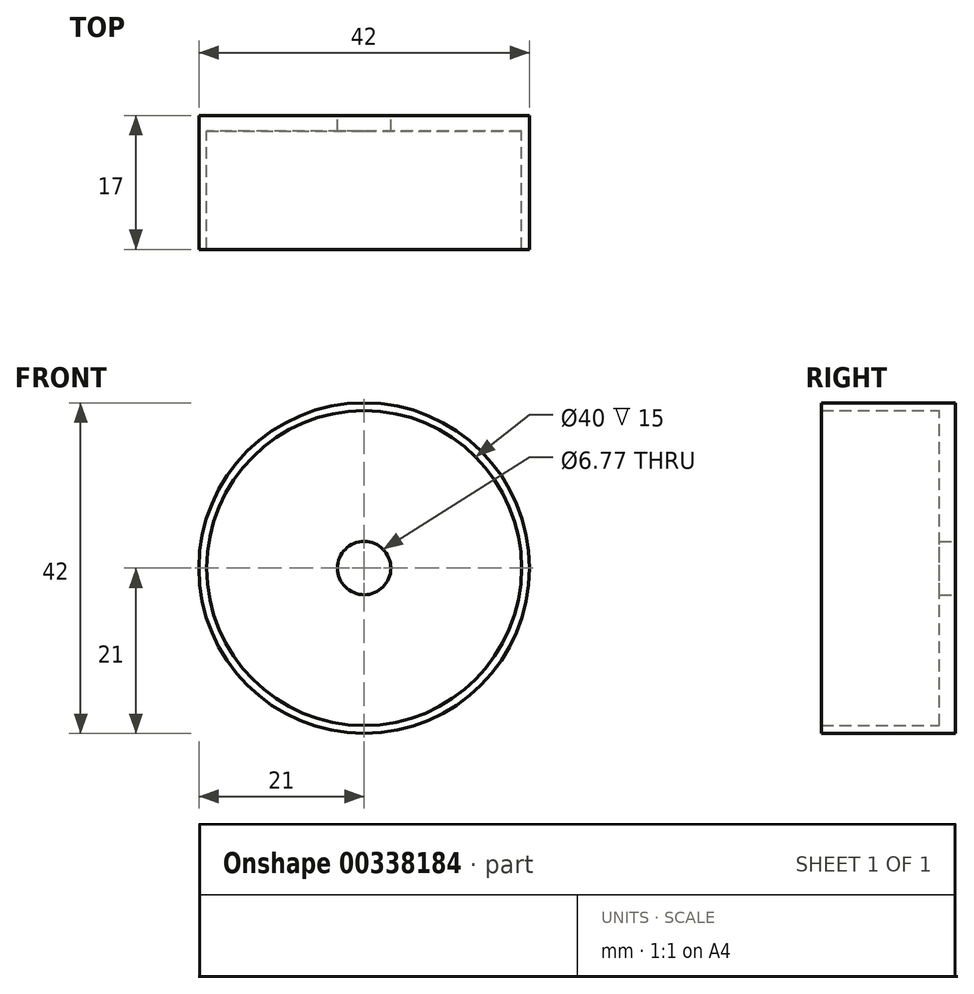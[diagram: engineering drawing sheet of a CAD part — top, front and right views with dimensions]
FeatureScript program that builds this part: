
annotation { "Feature Type Name" : "Feature", "Feature Type Description" : "" }
export const myFeature = defineFeature(function(context is Context, id is Id, definition is map)
    precondition{}
    {
        {
            var Q0;
            Q0=qCreatedBy(makeId("Front.planeOp"),FACE);
            var sketch = newSketch(context, id + "F0", { "sketchPlane" : qUnion([Q0])});
            skCircle(sketch, "E0", {"center": v(0, 0) * mm, "radius": 20 * mm});
            skCircle(sketch, "E1", {"center": v(0, 0) * mm, "radius": 21 * mm});
            skSolve(sketch);
        }
        {
            var Q0;
            Q0 = qSketchRegion(id + "F0", true);
            var Q1;
            Q1=makeQuery(id+"F0.imprint","IMPRINT",FACE,{"disambiguationData":[TD([[makeQuery(id+"F0.imprint","IMPRINT",EDGE,{"derivedFrom":sQuery(id+"F0.wireOp",EDGE,"E0")}),1.0]])]});
            var Q2;
            Q2 = qSketchRegion(id + "FLTfxNCL6GCXmSy_1", true);
            extrude(context, id + "F1", {"entities" : qUnion([Q0, Q1, Q2]), "oppositeDirection" : true, "depth" : 2 * mm});
        }
        {
            var Q0;
            Q0=makeQuery(id+"F1.opExtrude","CAP_FACE",FACE,{"disambiguationData":[OSD([sQuery(id+"F0.wireOp",EDGE,"E1")])],"isStart":true});
            var sketch = newSketch(context, id + "F2", { "sketchPlane" : qUnion([Q0])});
            skCircle(sketch, "E2", {"center": v(0, 0) * mm, "radius": 20 * mm});
            skSolve(sketch);
        }
        {
            var Q0;
            Q0=makeQuery(id+"F2.imprint","IMPRINT",FACE,{"disambiguationData":[TD([[makeQuery(id+"F2.imprint","IMPRINT",EDGE,{"derivedFrom":sQuery(id+"F2.wireOp",EDGE,"E2")}),-1.0]])]});
            extrude(context, id + "F3", {"entities" : qUnion([Q0]), "operationType" : NewBodyOperationType.ADD, "depth" : 15 * mm});
        }
        {
            var Q0;
            Q0=makeQuery(id+"F1.opExtrude","CAP_FACE",FACE,{"disambiguationData":[OSD([sQuery(id+"F0.wireOp",EDGE,"E1")])],"isStart":false});
            var sketch = newSketch(context, id + "F4", { "sketchPlane" : qUnion([Q0])});
            skCircle(sketch, "E3", {"center": v(0, 0) * mm, "radius": 3.38 * mm});
            skSolve(sketch);
        }
        {
            var Q0;
            Q0=makeQuery(id+"F4.imprint","IMPRINT",FACE,{"disambiguationData":[TD([[makeQuery(id+"F4.imprint","IMPRINT",EDGE,{"derivedFrom":sQuery(id+"F4.wireOp",EDGE,"E3")}),1.0]])]});
            extrude(context, id + "F5", {"entities" : qUnion([Q0]), "operationType" : NewBodyOperationType.REMOVE, "oppositeDirection" : true, "depth" : 25 * mm});
        }
    });
